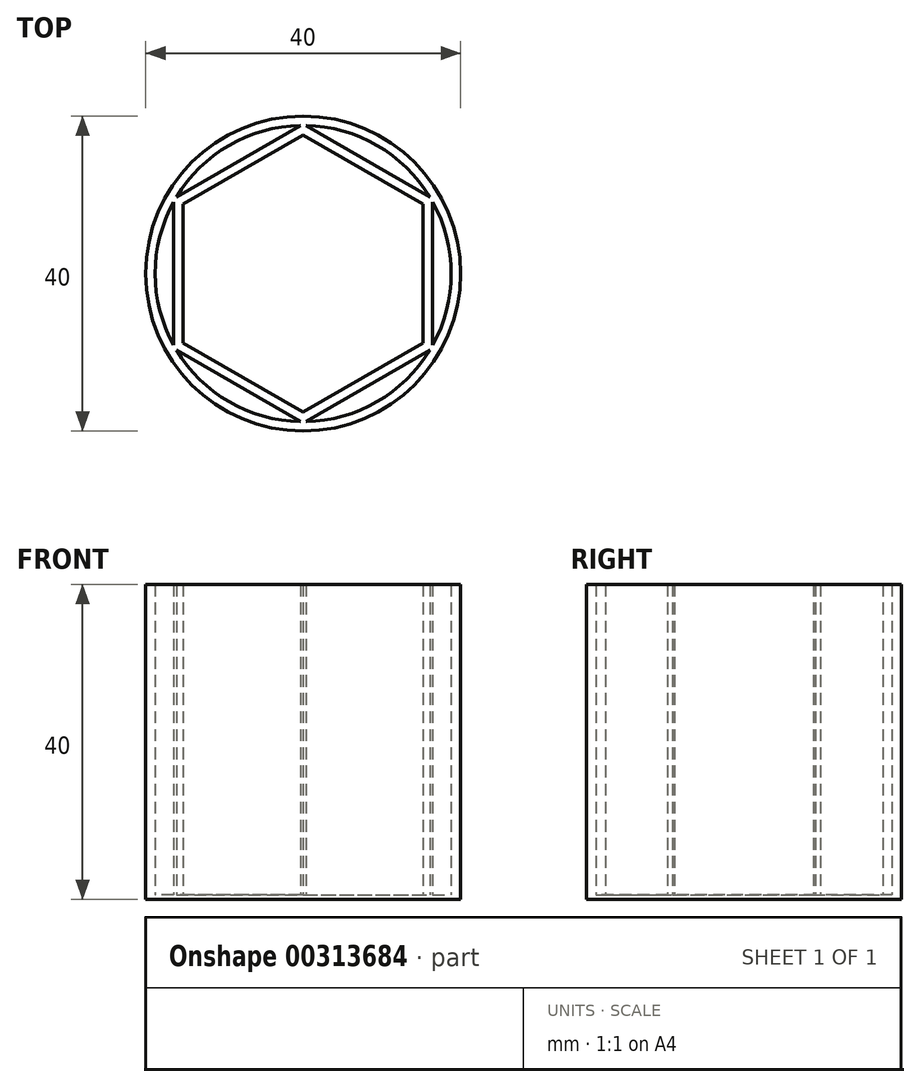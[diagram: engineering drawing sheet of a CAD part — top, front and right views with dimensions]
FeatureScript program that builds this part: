
annotation { "Feature Type Name" : "Feature", "Feature Type Description" : "" }
export const myFeature = defineFeature(function(context is Context, id is Id, definition is map)
    precondition{}
    {
        {
            var Q0;
            Q0=qCreatedBy(makeId("Top.planeOp"),FACE);
            var sketch = newSketch(context, id + "F0", { "sketchPlane" : qUnion([Q0])});
            skLineSegment(sketch, "E0.0", {"start": v(0.35, 18.8) * mm, "end": v(16.1, 9.7) * mm});
            skLineSegment(sketch, "E0.1", {"start": v(16.45, 9.1) * mm, "end": v(16.45, -9.1) * mm});
            skLineSegment(sketch, "E0.2", {"start": v(16.1, -9.7) * mm, "end": v(0.35, -18.8) * mm});
            skLineSegment(sketch, "E0.3", {"start": v(-0.35, -18.8) * mm, "end": v(-16.1, -9.7) * mm});
            skLineSegment(sketch, "E0.4", {"start": v(-16.45, -9.1) * mm, "end": v(-16.45, 9.1) * mm});
            skLineSegment(sketch, "E0.5", {"start": v(-16.1, 9.7) * mm, "end": v(-0.35, 18.8) * mm});
            skCircle(sketch, "E1", {"center": v(0, 0) * mm, "radius": 20 * mm});
            skCircle(sketch, "E2.cCircle", {"center": v(0, 0) * mm, "radius": 15.25 * mm, "construction": true});
            skLineSegment(sketch, "E2.0", {"start": v(-15.25, -8.8) * mm, "end": v(-15.25, 8.8) * mm});
            skLineSegment(sketch, "E2.1", {"start": v(-15.25, 8.8) * mm, "end": v(0, 17.61) * mm});
            skLineSegment(sketch, "E2.2", {"start": v(0, 17.61) * mm, "end": v(15.25, 8.8) * mm});
            skLineSegment(sketch, "E2.3", {"start": v(15.25, 8.8) * mm, "end": v(15.25, -8.8) * mm});
            skLineSegment(sketch, "E2.4", {"start": v(15.25, -8.8) * mm, "end": v(0, -17.61) * mm});
            skLineSegment(sketch, "E2.5", {"start": v(0, -17.61) * mm, "end": v(-15.25, -8.8) * mm});
            skPoint(sketch, "E2.0.midPoint", {"position": v(-15.25, 0) * mm});
            skCircle(sketch, "E3", {"center": v(0, 0) * mm, "radius": 18.8 * mm});
            skPoint(sketch, "E4.orphan", {"position": v(0, 19) * mm});
            skPoint(sketch, "E5.orphan", {"position": v(16.45, 9.5) * mm});
            skPoint(sketch, "E6.orphan", {"position": v(16.45, -9.5) * mm});
            skPoint(sketch, "E7.orphan", {"position": v(0, -19) * mm});
            skSolve(sketch);
        }
        {
            var Q0;
            {var subQ2=sQuery(id+"F0.wireOp",EDGE,"E0.0");Q0=makeQuery(id+"F0.imprint","IMPRINT",FACE,{"disambiguationData":[TD([[makeQuery(id+"F0.imprint","IMPRINT",EDGE,{"derivedFrom":subQ2}),-1.0]])]});}
            var Q1;
            Q1=makeQuery(id+"F0.imprint","IMPRINT",FACE,{"disambiguationData":[TD([[makeQuery(id+"F0.imprint","IMPRINT",EDGE,{"derivedFrom":sQuery(id+"F0.wireOp",EDGE,"E1")}),1.0]])]});
            extrude(context, id + "F1", {"entities" : qUnion([Q0, Q1]), "depth" : 40 * mm});
        }
        {
            var Q0;
            Q0=makeQuery(id+"F0.imprint","IMPRINT",FACE,{"disambiguationData":[TD([[makeQuery(id+"F0.imprint","IMPRINT",EDGE,{"derivedFrom":sQuery(id+"F0.wireOp",EDGE,"E1")}),1.0]])]});
            var Q1;
            {var subQ0=sQuery(id+"F0.wireOp",EDGE,"E0.0");Q1=makeQuery(id+"F0.imprint","IMPRINT",FACE,{"disambiguationData":[TD([[makeQuery(id+"F0.imprint","IMPRINT",EDGE,{"derivedFrom":subQ0}),1.0]])]});}
            var Q2;
            {var subQ2=sQuery(id+"F0.wireOp",EDGE,"E0.0");Q2=makeQuery(id+"F0.imprint","IMPRINT",FACE,{"disambiguationData":[TD([[makeQuery(id+"F0.imprint","IMPRINT",EDGE,{"derivedFrom":subQ2}),-1.0]])]});}
            var Q3;
            Q3=makeQuery(id+"F0.imprint","IMPRINT",FACE,{"disambiguationData":[TD([[makeQuery(id+"F0.imprint","IMPRINT",EDGE,{"derivedFrom":sQuery(id+"F0.wireOp",EDGE,"E2.0")}),-1.0]])]});
            var Q4;
            {var subQ0=sQuery(id+"F0.wireOp",EDGE,"E0.5");Q4=makeQuery(id+"F0.imprint","IMPRINT",FACE,{"disambiguationData":[TD([[makeQuery(id+"F0.imprint","IMPRINT",EDGE,{"derivedFrom":subQ0}),1.0]])]});}
            var Q5;
            {var subQ0=sQuery(id+"F0.wireOp",EDGE,"E0.4");Q5=makeQuery(id+"F0.imprint","IMPRINT",FACE,{"disambiguationData":[TD([[makeQuery(id+"F0.imprint","IMPRINT",EDGE,{"derivedFrom":subQ0}),1.0]])]});}
            var Q6;
            {var subQ0=sQuery(id+"F0.wireOp",EDGE,"E0.3");Q6=makeQuery(id+"F0.imprint","IMPRINT",FACE,{"disambiguationData":[TD([[makeQuery(id+"F0.imprint","IMPRINT",EDGE,{"derivedFrom":subQ0}),1.0]])]});}
            var Q7;
            {var subQ0=sQuery(id+"F0.wireOp",EDGE,"E0.2");Q7=makeQuery(id+"F0.imprint","IMPRINT",FACE,{"disambiguationData":[TD([[makeQuery(id+"F0.imprint","IMPRINT",EDGE,{"derivedFrom":subQ0}),1.0]])]});}
            var Q8;
            {var subQ0=sQuery(id+"F0.wireOp",EDGE,"E0.1");Q8=makeQuery(id+"F0.imprint","IMPRINT",FACE,{"disambiguationData":[TD([[makeQuery(id+"F0.imprint","IMPRINT",EDGE,{"derivedFrom":subQ0}),1.0]])]});}
            extrude(context, id + "F2", {"entities" : qUnion([Q0, Q1, Q2, Q3, Q4, Q5, Q6, Q7, Q8]), "operationType" : NewBodyOperationType.ADD, "depth" : 0.6 * mm});
        }
    });
